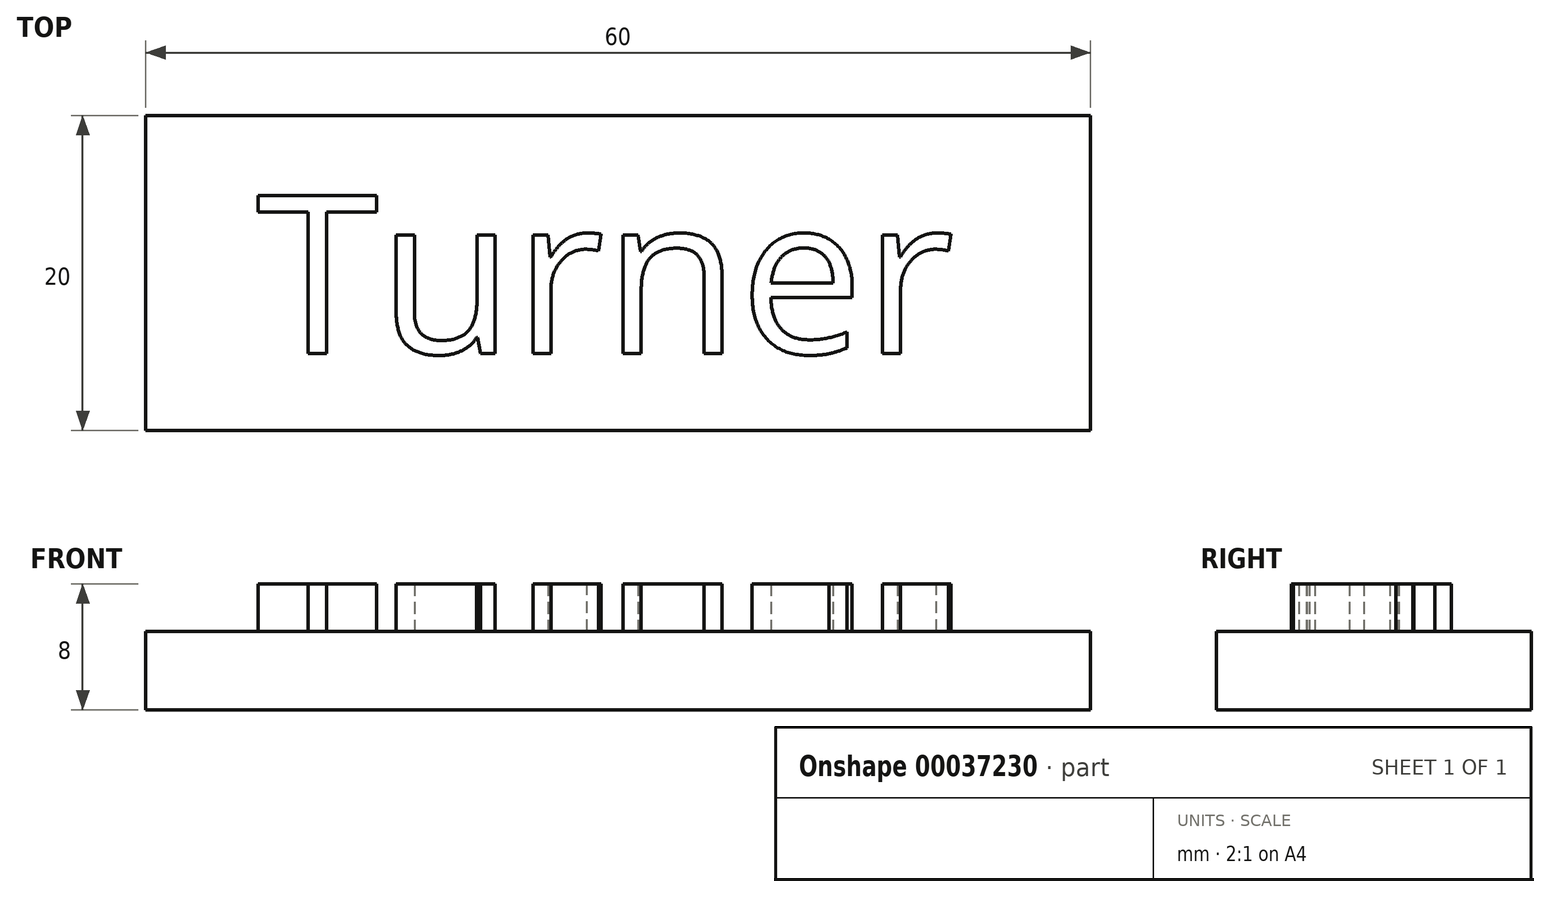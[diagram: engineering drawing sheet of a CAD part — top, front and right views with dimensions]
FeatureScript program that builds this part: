
annotation { "Feature Type Name" : "Feature", "Feature Type Description" : "" }
export const myFeature = defineFeature(function(context is Context, id is Id, definition is map)
    precondition{}
    {
        {
            var Q0;
            Q0=qCreatedBy(makeId("Top.planeOp"),FACE);
            var sketch = newSketch(context, id + "F0", { "sketchPlane" : qUnion([Q0])});
            skLineSegment(sketch, "E0.rect.bottom", {"start": v(30, -10) * mm, "end": v(-30, -10) * mm});
            skLineSegment(sketch, "E0.rect.top", {"start": v(30, 10) * mm, "end": v(-30, 10) * mm});
            skLineSegment(sketch, "E0.rect.left", {"start": v(30, -10) * mm, "end": v(30, 10) * mm});
            skLineSegment(sketch, "E0.rect.right", {"start": v(-30, -10) * mm, "end": v(-30, 10) * mm});
            skPoint(sketch, "E0.rect.middle", {"position": v(0, 0) * mm});
            skSolve(sketch);
        }
        {
            var Q0;
            Q0 = qSketchRegion(id + "F0", true);
            extrude(context, id + "F1", {"entities" : qUnion([Q0]), "depth" : 5 * mm});
        }
        {
            var Q0;
            Q0=makeQuery(id+"F1.opExtrude","CAP_FACE",FACE,{"disambiguationData":[OSD([sQuery(id+"F0.wireOp",EDGE,"E0.rect.bottom"),sQuery(id+"F0.wireOp",EDGE,"E0.rect.top"),sQuery(id+"F0.wireOp",EDGE,"E0.rect.left"),sQuery(id+"F0.wireOp",EDGE,"E0.rect.right")])],"isStart":false});
            var sketch = newSketch(context, id + "F2", { "sketchPlane" : qUnion([Q0])});
            skText(sketch, "E1", { "text": "Turner", "fontName": "OpenSans-Regular.ttf"});
            const initialGuessF2  = {"E1": [-0.02298, -0.0051, 1, 0, 0.0101]};
            skSetInitialGuess(sketch, initialGuessF2);
            skSolve(sketch);
        }
        {
            var Q0;
            Q0 = qSketchRegion(id + "F2", true);
            extrude(context, id + "F3", {"entities" : qUnion([Q0]), "operationType" : NewBodyOperationType.ADD, "depth" : 3 * mm});
        }
    });
